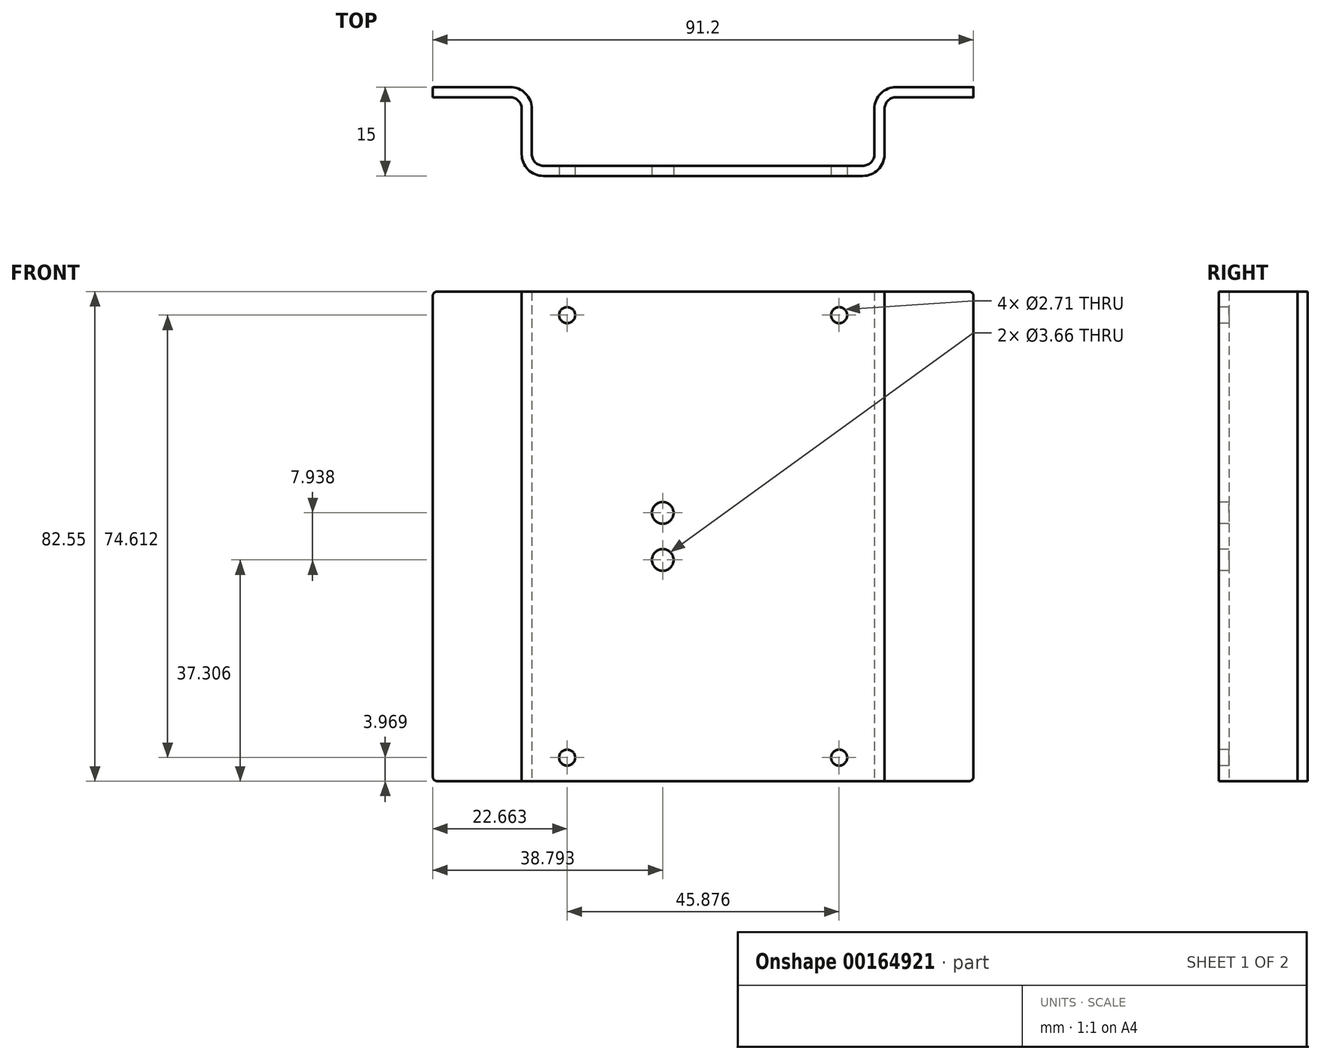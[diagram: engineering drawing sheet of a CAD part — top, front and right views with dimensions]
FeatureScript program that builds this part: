
annotation { "Feature Type Name" : "Feature", "Feature Type Description" : "" }
export const myFeature = defineFeature(function(context is Context, id is Id, definition is map)
    precondition{}
    {
        {
            var Q0;
            Q0=qCreatedBy(makeId("Top.planeOp"),FACE);
            var sketch = newSketch(context, id + "F0", { "sketchPlane" : qUnion([Q0])});
            skLineSegment(sketch, "E0", {"start": v(0, 0) * mm, "end": v(0, -13.3) * mm});
            skLineSegment(sketch, "E1", {"start": v(0, -13.3) * mm, "end": v(57.78, -13.3) * mm});
            skLineSegment(sketch, "E2", {"start": v(59.5, -15) * mm, "end": v(-1.7, -15) * mm});
            skLineSegment(sketch, "E3", {"start": v(-1.7, -15) * mm, "end": v(-1.7, -1.7) * mm});
            skLineSegment(sketch, "E4", {"start": v(0, -13.3) * mm, "end": v(-1.7, -13.3) * mm, "construction": true});
            skLineSegment(sketch, "E5", {"start": v(28.9, -15) * mm, "end": v(28.9, -13.3) * mm, "construction": true});
            skLineSegment(sketch, "E6", {"start": v(57.78, -13.3) * mm, "end": v(57.78, 0) * mm});
            skLineSegment(sketch, "E7", {"start": v(59.5, -1.7) * mm, "end": v(59.5, -15) * mm});
            skLineSegment(sketch, "E8", {"start": v(0, 0) * mm, "end": v(-16.7, 0) * mm});
            skLineSegment(sketch, "E9", {"start": v(-16.7, 0) * mm, "end": v(-16.7, -1.7) * mm});
            skLineSegment(sketch, "E10", {"start": v(-16.7, -1.7) * mm, "end": v(-1.7, -1.7) * mm});
            skLineSegment(sketch, "E11", {"start": v(59.5, -1.7) * mm, "end": v(74.5, -1.7) * mm});
            skLineSegment(sketch, "E12", {"start": v(74.5, -1.7) * mm, "end": v(74.5, 0) * mm});
            skLineSegment(sketch, "E13", {"start": v(74.5, 0) * mm, "end": v(57.78, 0) * mm});
            skPoint(sketch, "E14", {"position": v(-9.2, -1.7) * mm});
            skPoint(sketch, "E15", {"position": v(67, -1.7) * mm});
            skSolve(sketch);
        }
        {
            var Q0;
            Q0=qSketchRegion(id+"F0",true);
            extrude(context, id + "F1", {"entities" : qUnion([Q0]), "depth" : 82.55 * mm});
        }
        {
            var Q0;
            Q0=makeQuery(id+"F1.opExtrude","SWEPT_EDGE",EDGE,{"disambiguationData":[OSD([sQuery(id+"F0.wireOp",EDGE,"E2"),sQuery(id+"F0.wireOp",EDGE,"E7")])]});
            var Q1;
            Q1=makeQuery(id+"F1.opExtrude","SWEPT_EDGE",EDGE,{"disambiguationData":[OSD([sQuery(id+"F0.wireOp",EDGE,"E2"),sQuery(id+"F0.wireOp",EDGE,"E7")])]});
            var Q2;
            Q2=makeQuery(id+"F1.opExtrude","SWEPT_EDGE",EDGE,{"disambiguationData":[OSD([sQuery(id+"F0.wireOp",EDGE,"E2"),sQuery(id+"F0.wireOp",EDGE,"E3")])]});
            var Q3;
            Q3=makeQuery(id+"F1.opExtrude","SWEPT_EDGE",EDGE,{"disambiguationData":[OSD([sQuery(id+"F0.wireOp",EDGE,"E2"),sQuery(id+"F0.wireOp",EDGE,"E3")])]});
            var Q4;
            Q4=makeQuery(id+"F1.opExtrude","SWEPT_EDGE",EDGE,{"disambiguationData":[OSD([sQuery(id+"F0.wireOp",EDGE,"E0"),sQuery(id+"F0.wireOp",EDGE,"E8")])]});
            var Q5;
            Q5=makeQuery(id+"F1.opExtrude","SWEPT_EDGE",EDGE,{"disambiguationData":[OSD([sQuery(id+"F0.wireOp",EDGE,"E6"),sQuery(id+"F0.wireOp",EDGE,"E13")])]});
            fillet(context, id + "F2", {"entities" : qUnion([Q0, Q1, Q2, Q3, Q4, Q5]), "radius" : 3.7 * mm, "tangentPropagation" : true, "allowEdgeOverflow" : false});
        }
        {
            var Q0;
            Q0=makeQuery(id+"F1.opExtrude","SWEPT_EDGE",EDGE,{"disambiguationData":[OSD([sQuery(id+"F0.wireOp",EDGE,"E0"),sQuery(id+"F0.wireOp",EDGE,"E1")])]});
            var Q1;
            Q1=makeQuery(id+"F1.opExtrude","SWEPT_EDGE",EDGE,{"disambiguationData":[OSD([sQuery(id+"F0.wireOp",EDGE,"E1"),sQuery(id+"F0.wireOp",EDGE,"E6")])]});
            var Q2;
            Q2=makeQuery(id+"F1.opExtrude","SWEPT_EDGE",EDGE,{"disambiguationData":[OSD([sQuery(id+"F0.wireOp",EDGE,"E1"),sQuery(id+"F0.wireOp",EDGE,"E6")])]});
            var Q3;
            Q3=makeQuery(id+"F1.opExtrude","SWEPT_EDGE",EDGE,{"disambiguationData":[OSD([sQuery(id+"F0.wireOp",EDGE,"E0"),sQuery(id+"F0.wireOp",EDGE,"E1")])]});
            var Q4;
            Q4=makeQuery(id+"F1.opExtrude","SWEPT_EDGE",EDGE,{"disambiguationData":[OSD([sQuery(id+"F0.wireOp",EDGE,"E7"),sQuery(id+"F0.wireOp",EDGE,"E11")])]});
            var Q5;
            Q5=makeQuery(id+"F1.opExtrude","SWEPT_EDGE",EDGE,{"disambiguationData":[OSD([sQuery(id+"F0.wireOp",EDGE,"E3"),sQuery(id+"F0.wireOp",EDGE,"E10")])]});
            fillet(context, id + "F3", {"entities" : qUnion([Q0, Q1, Q2, Q3, Q4, Q5]), "radius" : 1.98 * mm, "tangentPropagation" : true, "allowEdgeOverflow" : false});
        }
        {
            var Q0;
            Q0=makeQuery(id+"F1.opExtrude","SWEPT_FACE",FACE,{"disambiguationData":[OSD([sQuery(id+"F0.wireOp",EDGE,"E2")])]});
            var sketch = newSketch(context, id + "F4", { "sketchPlane" : qUnion([Q0])});
            skLineSegment(sketch, "E16", {"start": v(55.8, 41.28) * mm, "end": v(51.83, 41.28) * mm, "construction": true});
            skLineSegment(sketch, "E17.bottom", {"start": v(51.83, 78.58) * mm, "end": v(5.95, 78.58) * mm, "construction": true});
            skLineSegment(sketch, "E17.top", {"start": v(51.83, 3.97) * mm, "end": v(5.95, 3.97) * mm, "construction": true});
            skLineSegment(sketch, "E17.left", {"start": v(51.83, 78.58) * mm, "end": v(51.83, 3.97) * mm, "construction": true});
            skLineSegment(sketch, "E17.right", {"start": v(5.95, 78.58) * mm, "end": v(5.95, 3.97) * mm, "construction": true});
            skCircle(sketch, "E18", {"center": v(51.83, 78.58) * mm, "radius": 1.35 * mm});
            skCircle(sketch, "E19", {"center": v(5.95, 78.58) * mm, "radius": 1.35 * mm});
            skCircle(sketch, "E20", {"center": v(5.95, 3.97) * mm, "radius": 1.35 * mm});
            skCircle(sketch, "E21", {"center": v(51.83, 3.97) * mm, "radius": 1.35 * mm});
            skLineSegment(sketch, "E22", {"start": v(5.95, 41.27) * mm, "end": v(1.98, 41.27) * mm, "construction": true});
            skLineSegment(sketch, "E23", {"start": v(28.9, 3.97) * mm, "end": v(28.9, 0) * mm, "construction": true});
            skLineSegment(sketch, "E24", {"start": v(22.08, 37.3) * mm, "end": v(22.08, 45.24) * mm, "construction": true});
            skCircle(sketch, "E25", {"center": v(22.08, 37.3) * mm, "radius": 1.83 * mm});
            skCircle(sketch, "E26", {"center": v(22.08, 45.24) * mm, "radius": 1.83 * mm});
            skLineSegment(sketch, "E27", {"start": v(28.9, 78.58) * mm, "end": v(28.9, 3.97) * mm, "construction": true});
            skLineSegment(sketch, "E28", {"start": v(28.9, 41.28) * mm, "end": v(22.08, 41.28) * mm, "construction": true});
            skSolve(sketch);
        }
        {
            var Q0;
            Q0=qSketchRegion(id+"F4",true);
            var Q1;
            Q1=makeQuery(id+"F1.opExtrude","SWEPT_FACE",FACE,{"disambiguationData":[OSD([sQuery(id+"F0.wireOp",EDGE,"E1")])]});
            extrude(context, id + "F5", {"entities" : qUnion([Q0]), "operationType" : NewBodyOperationType.REMOVE, "endBound" : BoundingType.UP_TO_SURFACE, "oppositeDirection" : true, "endBoundEntityFace" : qUnion([Q1]), "depth" : 25.4 * mm});
        }
        {
            var Q0;
            Q0=makeQuery(id+"F1.opExtrude","CAP_EDGE",EDGE,{"disambiguationData":[OSD([sQuery(id+"F0.wireOp",EDGE,"E9")])],"isStart":false});
            var Q1;
            Q1=makeQuery(id+"F1.opExtrude","CAP_EDGE",EDGE,{"disambiguationData":[OSD([sQuery(id+"F0.wireOp",EDGE,"E9")])],"isStart":true});
            var Q2;
            Q2=makeQuery(id+"F1.opExtrude","CAP_EDGE",EDGE,{"disambiguationData":[OSD([sQuery(id+"F0.wireOp",EDGE,"E12")])],"isStart":true});
            var Q3;
            Q3=makeQuery(id+"F1.opExtrude","CAP_EDGE",EDGE,{"disambiguationData":[OSD([sQuery(id+"F0.wireOp",EDGE,"E12")])],"isStart":false});
            fillet(context, id + "F6", {"entities" : qUnion([Q0, Q1, Q2, Q3]), "radius" : 0.76 * mm, "tangentPropagation" : true, "allowEdgeOverflow" : false});
        }
    });
